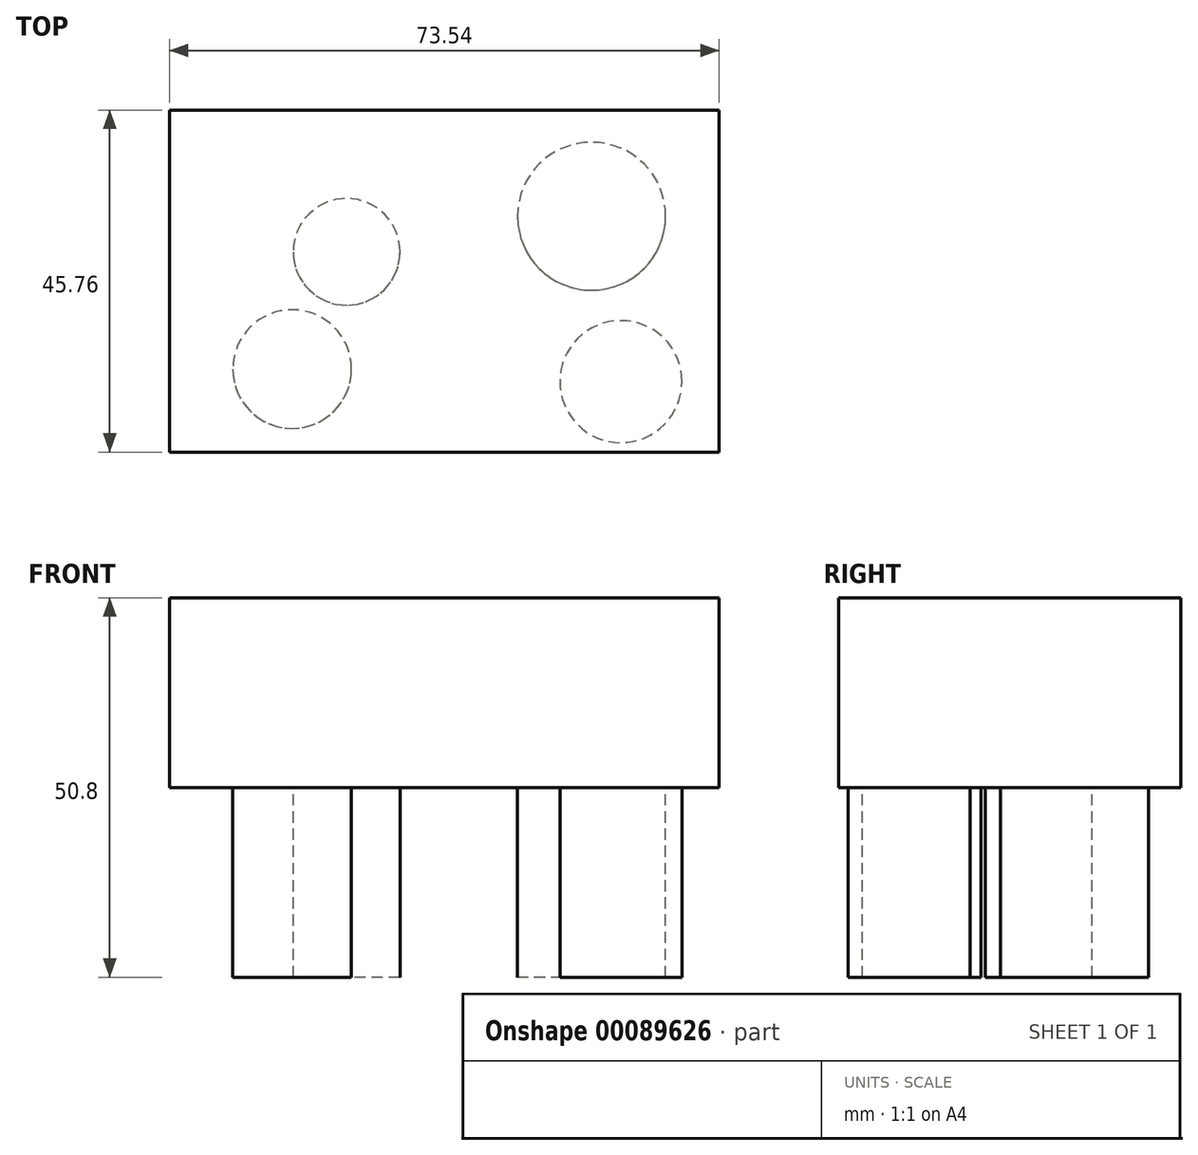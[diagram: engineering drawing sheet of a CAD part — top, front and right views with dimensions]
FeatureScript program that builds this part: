
annotation { "Feature Type Name" : "Feature", "Feature Type Description" : "" }
export const myFeature = defineFeature(function(context is Context, id is Id, definition is map)
    precondition{}
    {
        {
            var Q0;
            Q0=qCreatedBy(makeId("Top.planeOp"),FACE);
            var sketch = newSketch(context, id + "F0", { "sketchPlane" : qUnion([Q0])});
            skLineSegment(sketch, "E0.bottom", {"start": v(-36.73, 25.41) * mm, "end": v(36.81, 25.41) * mm});
            skLineSegment(sketch, "E0.top", {"start": v(-36.73, -20.35) * mm, "end": v(36.81, -20.35) * mm});
            skLineSegment(sketch, "E0.left", {"start": v(-36.73, 25.41) * mm, "end": v(-36.73, -20.35) * mm});
            skLineSegment(sketch, "E0.right", {"start": v(36.81, 25.41) * mm, "end": v(36.81, -20.35) * mm});
            skSolve(sketch);
        }
        {
            var Q0;
            Q0=makeQuery(id+"F0.imprint","IMPRINT",FACE,{"disambiguationData":[TD([[makeQuery(id+"F0.imprint","IMPRINT",EDGE,{"derivedFrom":sQuery(id+"F0.wireOp",EDGE,"E0.bottom")}),-1.0]])]});
            extrude(context, id + "F1", {"entities" : qUnion([Q0]), "depth" : 12.7 * mm, "hasSecondDirection" : true, "secondDirectionOppositeDirection" : true, "secondDirectionDepth" : 12.7 * mm});
        }
        {
            var Q0;
            Q0=makeQuery(id+"F1.opExtrude","CAP_FACE",FACE,{"disambiguationData":[OSD([sQuery(id+"F0.wireOp",EDGE,"E0.bottom"),sQuery(id+"F0.wireOp",EDGE,"E0.top"),sQuery(id+"F0.wireOp",EDGE,"E0.left"),sQuery(id+"F0.wireOp",EDGE,"E0.right")])],"isStart":true});
            var sketch = newSketch(context, id + "F2", { "sketchPlane" : qUnion([Q0])});
            skCircle(sketch, "E1", {"center": v(23.68, 10.93) * mm, "radius": 8.17 * mm});
            skSolve(sketch);
        }
        {
            var Q0;
            Q0 = qSketchRegion(id + "F2", true);
            extrude(context, id + "F3", {"entities" : qUnion([Q0]), "operationType" : NewBodyOperationType.ADD, "depth" : 25.4 * mm});
        }
        {
            var Q0;
            Q0=makeQuery(id+"F1.opExtrude","CAP_FACE",FACE,{"disambiguationData":[OSD([sQuery(id+"F0.wireOp",EDGE,"E0.bottom"),sQuery(id+"F0.wireOp",EDGE,"E0.top"),sQuery(id+"F0.wireOp",EDGE,"E0.left"),sQuery(id+"F0.wireOp",EDGE,"E0.right")])],"isStart":true});
            var sketch = newSketch(context, id + "F4", { "sketchPlane" : qUnion([Q0])});
            skCircle(sketch, "E2", {"center": v(19.76, -11.2) * mm, "radius": 9.9 * mm});
            skSolve(sketch);
        }
        {
            var Q0;
            Q0 = qSketchRegion(id + "F4", true);
            extrude(context, id + "F5", {"entities" : qUnion([Q0]), "operationType" : NewBodyOperationType.ADD, "depth" : 25.4 * mm});
        }
        {
            var Q0;
            Q0=makeQuery(id+"F1.opExtrude","CAP_FACE",FACE,{"disambiguationData":[OSD([sQuery(id+"F0.wireOp",EDGE,"E0.bottom"),sQuery(id+"F0.wireOp",EDGE,"E0.top"),sQuery(id+"F0.wireOp",EDGE,"E0.left"),sQuery(id+"F0.wireOp",EDGE,"E0.right")])],"isStart":true});
            var sketch = newSketch(context, id + "F6", { "sketchPlane" : qUnion([Q0])});
            skCircle(sketch, "E3", {"center": v(-20.32, 9.25) * mm, "radius": 7.94 * mm});
            skSolve(sketch);
        }
        {
            var Q0;
            Q0 = qSketchRegion(id + "F6", true);
            extrude(context, id + "F7", {"entities" : qUnion([Q0]), "operationType" : NewBodyOperationType.ADD, "depth" : 25.4 * mm});
        }
        {
            var Q0;
            Q0=makeQuery(id+"F1.opExtrude","CAP_FACE",FACE,{"disambiguationData":[OSD([sQuery(id+"F0.wireOp",EDGE,"E0.bottom"),sQuery(id+"F0.wireOp",EDGE,"E0.top"),sQuery(id+"F0.wireOp",EDGE,"E0.left"),sQuery(id+"F0.wireOp",EDGE,"E0.right")])],"isStart":true});
            var sketch = newSketch(context, id + "F8", { "sketchPlane" : qUnion([Q0])});
            skCircle(sketch, "E4", {"center": v(-13.03, -6.45) * mm, "radius": 7.14 * mm});
            skSolve(sketch);
        }
        {
            var Q0;
            Q0 = qSketchRegion(id + "F8", true);
            extrude(context, id + "F9", {"entities" : qUnion([Q0]), "operationType" : NewBodyOperationType.ADD, "depth" : 25.4 * mm});
        }
    });
